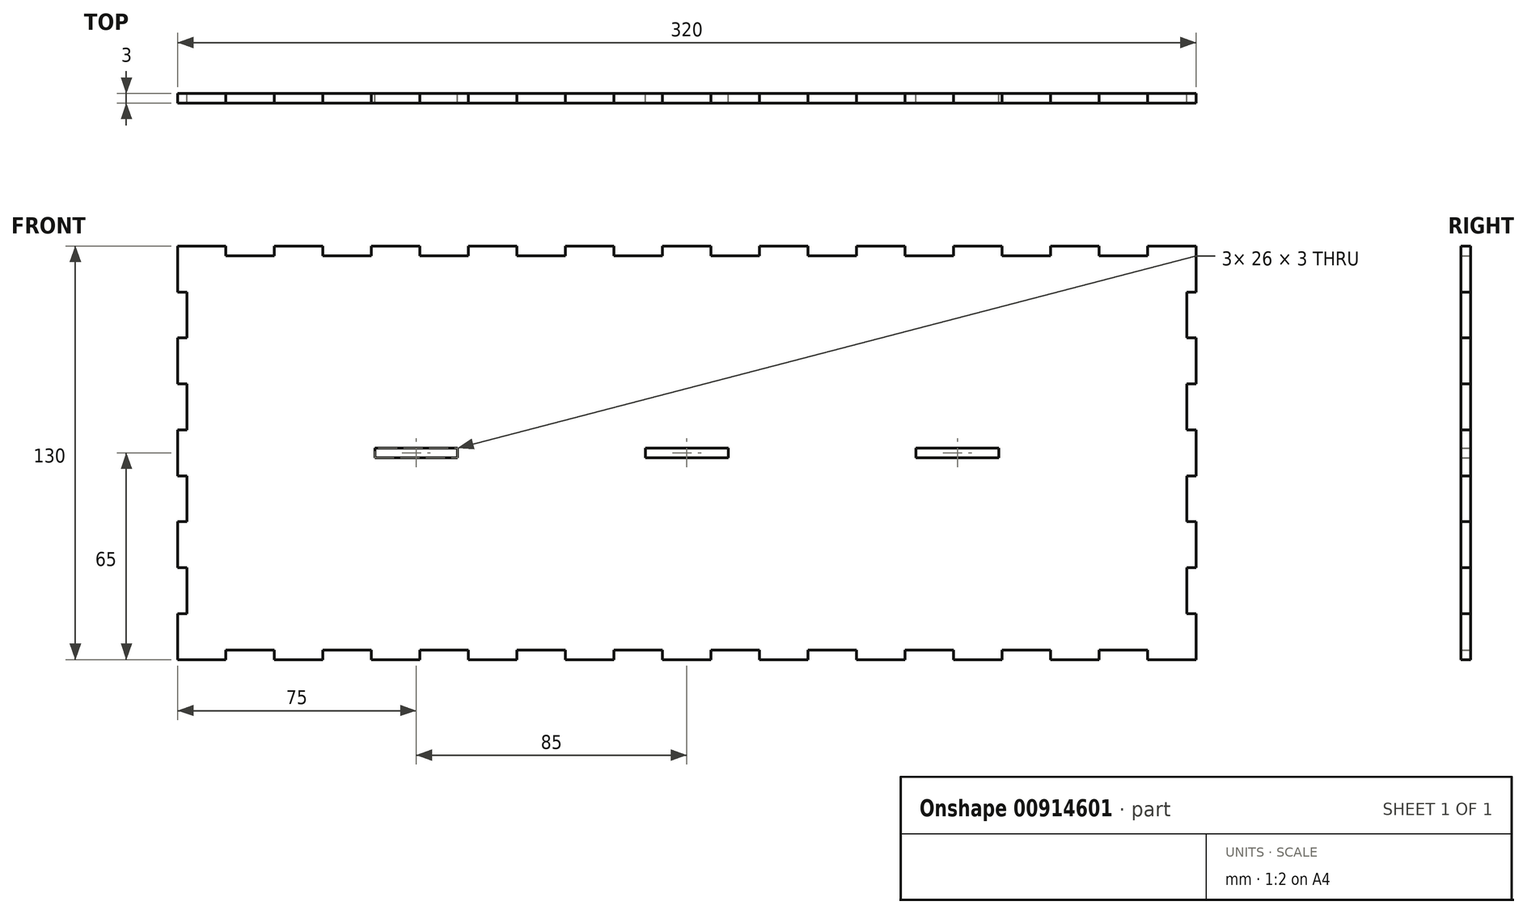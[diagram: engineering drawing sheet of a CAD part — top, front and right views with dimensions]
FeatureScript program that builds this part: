
annotation { "Feature Type Name" : "Feature", "Feature Type Description" : "" }
export const myFeature = defineFeature(function(context is Context, id is Id, definition is map)
    precondition{}
    {
        {
            var Q0;
            Q0=qCreatedBy(makeId("Front.planeOp"),FACE);
            var sketch = newSketch(context, id + "F0", { "sketchPlane" : qUnion([Q0])});
            skLineSegment(sketch, "E0.top", {"start": v(160, 65) * mm, "end": v(144.76, 65) * mm});
            skLineSegment(sketch, "E0.left", {"start": v(160, -65) * mm, "end": v(160, -62) * mm});
            skLineSegment(sketch, "E0.right", {"start": v(-160, -65) * mm, "end": v(-160, -50.56) * mm});
            skPoint(sketch, "E0.middle", {"position": v(0, 0) * mm});
            skLineSegment(sketch, "E1", {"start": v(-144.76, 62) * mm, "end": v(-129.52, 62) * mm});
            skLineSegment(sketch, "E2", {"start": v(-144.76, 65) * mm, "end": v(-144.76, 62) * mm});
            skLineSegment(sketch, "E3", {"start": v(-129.52, 65) * mm, "end": v(-129.52, 62) * mm});
            skLineSegment(sketch, "E4", {"start": v(-99.05, 65) * mm, "end": v(-99.05, 62) * mm});
            skLineSegment(sketch, "E5", {"start": v(-114.29, 65) * mm, "end": v(-114.29, 62) * mm});
            skLineSegment(sketch, "E6", {"start": v(-83.8, 65) * mm, "end": v(-83.8, 62) * mm});
            skLineSegment(sketch, "E7", {"start": v(-68.57, 65) * mm, "end": v(-68.57, 62) * mm});
            skLineSegment(sketch, "E8", {"start": v(-53.33, 65) * mm, "end": v(-53.33, 62) * mm});
            skLineSegment(sketch, "E9", {"start": v(-38.1, 65) * mm, "end": v(-38.1, 62) * mm});
            skLineSegment(sketch, "E10", {"start": v(-22.86, 65) * mm, "end": v(-22.86, 62) * mm});
            skLineSegment(sketch, "E11", {"start": v(22.86, 65) * mm, "end": v(22.86, 62) * mm});
            skLineSegment(sketch, "E12", {"start": v(-7.62, 65) * mm, "end": v(-7.62, 62) * mm});
            skLineSegment(sketch, "E13", {"start": v(7.62, 65) * mm, "end": v(7.62, 62) * mm});
            skLineSegment(sketch, "E14", {"start": v(38.1, 65) * mm, "end": v(38.1, 62) * mm});
            skLineSegment(sketch, "E15", {"start": v(53.33, 65) * mm, "end": v(53.33, 62) * mm});
            skLineSegment(sketch, "E16", {"start": v(68.57, 65) * mm, "end": v(68.57, 62) * mm});
            skLineSegment(sketch, "E17", {"start": v(83.8, 65) * mm, "end": v(83.8, 62) * mm});
            skLineSegment(sketch, "E18", {"start": v(99.05, 65) * mm, "end": v(99.05, 62) * mm});
            skLineSegment(sketch, "E19", {"start": v(114.29, 65) * mm, "end": v(114.29, 62) * mm});
            skLineSegment(sketch, "E20", {"start": v(129.52, 65) * mm, "end": v(129.52, 62) * mm});
            skLineSegment(sketch, "E21", {"start": v(144.76, 65) * mm, "end": v(144.76, 62) * mm});
            skLineSegment(sketch, "E22.trimOffspring", {"start": v(-144.76, 65) * mm, "end": v(-160, 65) * mm});
            skLineSegment(sketch, "E23.trimOffspring", {"start": v(-114.29, 62) * mm, "end": v(-99.05, 62) * mm});
            skLineSegment(sketch, "E24.trimOffspring", {"start": v(-114.29, 65) * mm, "end": v(-129.52, 65) * mm});
            skLineSegment(sketch, "E25.trimOffspring", {"start": v(-83.8, 62) * mm, "end": v(-68.57, 62) * mm});
            skLineSegment(sketch, "E26.trimOffspring", {"start": v(-83.8, 65) * mm, "end": v(-99.05, 65) * mm});
            skLineSegment(sketch, "E27.trimOffspring", {"start": v(-53.33, 62) * mm, "end": v(-38.1, 62) * mm});
            skLineSegment(sketch, "E28.trimOffspring", {"start": v(-53.33, 65) * mm, "end": v(-68.57, 65) * mm});
            skLineSegment(sketch, "E29.trimOffspring", {"start": v(-22.86, 62) * mm, "end": v(-7.62, 62) * mm});
            skLineSegment(sketch, "E30.trimOffspring", {"start": v(-22.86, 65) * mm, "end": v(-38.1, 65) * mm});
            skLineSegment(sketch, "E31.trimOffspring", {"start": v(7.62, 62) * mm, "end": v(22.86, 62) * mm});
            skLineSegment(sketch, "E32.trimOffspring", {"start": v(7.62, 65) * mm, "end": v(-7.62, 65) * mm});
            skLineSegment(sketch, "E33.trimOffspring", {"start": v(38.1, 62) * mm, "end": v(53.33, 62) * mm});
            skLineSegment(sketch, "E34.trimOffspring", {"start": v(38.1, 65) * mm, "end": v(22.86, 65) * mm});
            skLineSegment(sketch, "E35.trimOffspring", {"start": v(68.57, 62) * mm, "end": v(83.8, 62) * mm});
            skLineSegment(sketch, "E36.trimOffspring", {"start": v(68.57, 65) * mm, "end": v(53.33, 65) * mm});
            skLineSegment(sketch, "E37.trimOffspring", {"start": v(99.05, 62) * mm, "end": v(114.29, 62) * mm});
            skLineSegment(sketch, "E38.trimOffspring", {"start": v(99.05, 65) * mm, "end": v(83.8, 65) * mm});
            skLineSegment(sketch, "E39.trimOffspring", {"start": v(129.52, 62) * mm, "end": v(144.76, 62) * mm});
            skLineSegment(sketch, "E40.trimOffspring", {"start": v(129.52, 65) * mm, "end": v(114.29, 65) * mm});
            skLineSegment(sketch, "E41.MirrorCS", {"start": v(-38.1, -65) * mm, "end": v(-38.1, -62) * mm});
            skLineSegment(sketch, "E42.MirrorCS", {"start": v(-7.62, -65) * mm, "end": v(-7.62, -62) * mm});
            skLineSegment(sketch, "E43.MirrorCS", {"start": v(-22.86, -65) * mm, "end": v(-22.86, -62) * mm});
            skLineSegment(sketch, "E44.MirrorCS", {"start": v(53.33, -65) * mm, "end": v(53.33, -62) * mm});
            skLineSegment(sketch, "E45.MirrorCS", {"start": v(99.05, -65) * mm, "end": v(99.05, -62) * mm});
            skLineSegment(sketch, "E46.MirrorCS", {"start": v(-114.29, -65) * mm, "end": v(-114.29, -62) * mm});
            skLineSegment(sketch, "E47.MirrorCS", {"start": v(38.1, -65) * mm, "end": v(38.1, -62) * mm});
            skLineSegment(sketch, "E48.MirrorCS", {"start": v(-99.05, -65) * mm, "end": v(-99.05, -62) * mm});
            skLineSegment(sketch, "E49.MirrorCS", {"start": v(-68.57, -65) * mm, "end": v(-68.57, -62) * mm});
            skLineSegment(sketch, "E50.MirrorCS", {"start": v(-129.52, -65) * mm, "end": v(-129.52, -62) * mm});
            skLineSegment(sketch, "E51.MirrorCS", {"start": v(114.29, -65) * mm, "end": v(114.29, -62) * mm});
            skLineSegment(sketch, "E52.MirrorCS", {"start": v(-144.76, -65) * mm, "end": v(-144.76, -62) * mm});
            skLineSegment(sketch, "E53.MirrorCS", {"start": v(83.8, -65) * mm, "end": v(83.8, -62) * mm});
            skLineSegment(sketch, "E54.MirrorCS", {"start": v(129.52, -65) * mm, "end": v(129.52, -62) * mm});
            skLineSegment(sketch, "E55.MirrorCS", {"start": v(7.62, -65) * mm, "end": v(7.62, -62) * mm});
            skLineSegment(sketch, "E56.MirrorCS", {"start": v(144.76, -65) * mm, "end": v(144.76, -62) * mm});
            skLineSegment(sketch, "E57.MirrorCS", {"start": v(68.57, -65) * mm, "end": v(68.57, -62) * mm});
            skLineSegment(sketch, "E58.MirrorCS", {"start": v(22.86, -65) * mm, "end": v(22.86, -62) * mm});
            skLineSegment(sketch, "E59.MirrorCS", {"start": v(-83.8, -65) * mm, "end": v(-83.8, -62) * mm});
            skLineSegment(sketch, "E60.MirrorCS", {"start": v(-53.33, -65) * mm, "end": v(-53.33, -62) * mm});
            skLineSegment(sketch, "E61.MirrorCS", {"start": v(-22.86, -62) * mm, "end": v(-7.62, -62) * mm});
            skLineSegment(sketch, "E62.MirrorCS", {"start": v(-144.76, -65) * mm, "end": v(-160, -65) * mm});
            skLineSegment(sketch, "E63.MirrorCS", {"start": v(-22.86, -65) * mm, "end": v(-38.1, -65) * mm});
            skLineSegment(sketch, "E64.MirrorCS", {"start": v(-53.33, -62) * mm, "end": v(-38.1, -62) * mm});
            skLineSegment(sketch, "E65.MirrorCS", {"start": v(-144.76, -62) * mm, "end": v(-129.52, -62) * mm});
            skLineSegment(sketch, "E66.MirrorCS", {"start": v(129.52, -62) * mm, "end": v(144.76, -62) * mm});
            skLineSegment(sketch, "E67.MirrorCS", {"start": v(-114.29, -62) * mm, "end": v(-99.05, -62) * mm});
            skLineSegment(sketch, "E68.MirrorCS", {"start": v(7.62, -65) * mm, "end": v(-7.62, -65) * mm});
            skLineSegment(sketch, "E69.MirrorCS", {"start": v(38.1, -62) * mm, "end": v(53.33, -62) * mm});
            skLineSegment(sketch, "E70.MirrorCS", {"start": v(68.57, -62) * mm, "end": v(83.8, -62) * mm});
            skLineSegment(sketch, "E71.MirrorCS", {"start": v(99.05, -62) * mm, "end": v(114.29, -62) * mm});
            skLineSegment(sketch, "E72.MirrorCS", {"start": v(68.57, -65) * mm, "end": v(53.33, -65) * mm});
            skLineSegment(sketch, "E73.MirrorCS", {"start": v(-114.29, -65) * mm, "end": v(-129.52, -65) * mm});
            skLineSegment(sketch, "E74.MirrorCS", {"start": v(99.05, -65) * mm, "end": v(83.8, -65) * mm});
            skLineSegment(sketch, "E75.MirrorCS", {"start": v(129.52, -65) * mm, "end": v(114.29, -65) * mm});
            skLineSegment(sketch, "E76.MirrorCS", {"start": v(-53.33, -65) * mm, "end": v(-68.57, -65) * mm});
            skLineSegment(sketch, "E77.MirrorCS", {"start": v(-83.8, -62) * mm, "end": v(-68.57, -62) * mm});
            skLineSegment(sketch, "E78.MirrorCS", {"start": v(38.1, -65) * mm, "end": v(22.86, -65) * mm});
            skLineSegment(sketch, "E79.MirrorCS", {"start": v(-83.8, -65) * mm, "end": v(-99.05, -65) * mm});
            skLineSegment(sketch, "E80.MirrorCS", {"start": v(7.62, -62) * mm, "end": v(22.86, -62) * mm});
            skLineSegment(sketch, "E81.MirrorCS", {"start": v(160, -65) * mm, "end": v(144.76, -65) * mm});
            skLineSegment(sketch, "E82", {"start": v(-157, 50.56) * mm, "end": v(-157, 36.11) * mm});
            skLineSegment(sketch, "E83", {"start": v(-160, 50.56) * mm, "end": v(-157, 50.56) * mm});
            skLineSegment(sketch, "E84", {"start": v(-160, 36.11) * mm, "end": v(-157, 36.11) * mm});
            skLineSegment(sketch, "E85", {"start": v(-160, 21.67) * mm, "end": v(-157, 21.67) * mm});
            skLineSegment(sketch, "E86", {"start": v(-160, 7.22) * mm, "end": v(-157, 7.22) * mm});
            skLineSegment(sketch, "E87", {"start": v(-160, -7.22) * mm, "end": v(-157, -7.22) * mm});
            skLineSegment(sketch, "E88", {"start": v(-160, -21.67) * mm, "end": v(-157, -21.67) * mm});
            skLineSegment(sketch, "E89", {"start": v(-160, -36.11) * mm, "end": v(-157, -36.11) * mm});
            skLineSegment(sketch, "E90", {"start": v(-160, -50.56) * mm, "end": v(-157, -50.56) * mm});
            skLineSegment(sketch, "E91.trimOffspring", {"start": v(-160, 50.56) * mm, "end": v(-160, 65) * mm});
            skLineSegment(sketch, "E92.trimOffspring", {"start": v(-157, 21.67) * mm, "end": v(-157, 7.22) * mm});
            skLineSegment(sketch, "E93.trimOffspring", {"start": v(-160, 21.67) * mm, "end": v(-160, 36.11) * mm});
            skLineSegment(sketch, "E94.trimOffspring", {"start": v(-157, -7.22) * mm, "end": v(-157, -21.67) * mm});
            skLineSegment(sketch, "E95.trimOffspring", {"start": v(-160, -7.22) * mm, "end": v(-160, 7.22) * mm});
            skLineSegment(sketch, "E96.trimOffspring", {"start": v(-157, -36.11) * mm, "end": v(-157, -50.56) * mm});
            skLineSegment(sketch, "E97.trimOffspring", {"start": v(-160, -36.11) * mm, "end": v(-160, -21.67) * mm});
            skLineSegment(sketch, "E98.trimOffspring", {"start": v(160, 62) * mm, "end": v(160, 65) * mm});
            skLineSegment(sketch, "E99.MirrorCS", {"start": v(160, -36.11) * mm, "end": v(157, -36.11) * mm});
            skLineSegment(sketch, "E100.MirrorCS", {"start": v(160, 50.56) * mm, "end": v(157, 50.56) * mm});
            skLineSegment(sketch, "E101.MirrorCS", {"start": v(160, -21.67) * mm, "end": v(157, -21.67) * mm});
            skLineSegment(sketch, "E102.MirrorCS", {"start": v(160, -7.22) * mm, "end": v(157, -7.22) * mm});
            skLineSegment(sketch, "E103.MirrorCS", {"start": v(160, -50.56) * mm, "end": v(157, -50.56) * mm});
            skLineSegment(sketch, "E104.MirrorCS", {"start": v(160, 21.67) * mm, "end": v(157, 21.67) * mm});
            skLineSegment(sketch, "E105.MirrorCS", {"start": v(160, 36.11) * mm, "end": v(157, 36.11) * mm});
            skLineSegment(sketch, "E106.MirrorCS", {"start": v(160, 7.22) * mm, "end": v(157, 7.22) * mm});
            skLineSegment(sketch, "E107.MirrorCS", {"start": v(160, 21.67) * mm, "end": v(160, 36.11) * mm});
            skLineSegment(sketch, "E108.MirrorCS", {"start": v(160, -36.11) * mm, "end": v(160, -21.67) * mm});
            skLineSegment(sketch, "E109.MirrorCS", {"start": v(160, -7.22) * mm, "end": v(160, 7.22) * mm});
            skLineSegment(sketch, "E110.MirrorCS", {"start": v(157, 21.67) * mm, "end": v(157, 7.22) * mm});
            skLineSegment(sketch, "E111.MirrorCS", {"start": v(157, -7.22) * mm, "end": v(157, -21.67) * mm});
            skLineSegment(sketch, "E112.MirrorCS", {"start": v(160, 50.56) * mm, "end": v(160, 65) * mm});
            skLineSegment(sketch, "E113.MirrorCS", {"start": v(157, 50.56) * mm, "end": v(157, 36.11) * mm});
            skLineSegment(sketch, "E114.MirrorCS", {"start": v(160, -65) * mm, "end": v(160, -50.56) * mm});
            skLineSegment(sketch, "E115.MirrorCS", {"start": v(157, -36.11) * mm, "end": v(157, -50.56) * mm});
            skLineSegment(sketch, "E116.bottom", {"start": v(98, -1.5) * mm, "end": v(72, -1.5) * mm});
            skLineSegment(sketch, "E116.top", {"start": v(98, 1.5) * mm, "end": v(72, 1.5) * mm});
            skLineSegment(sketch, "E116.left", {"start": v(160, -1.5) * mm, "end": v(160, 1.5) * mm});
            skLineSegment(sketch, "E116.right", {"start": v(-160, -1.5) * mm, "end": v(-160, 1.5) * mm});
            skLineSegment(sketch, "E117", {"start": v(-13, 1.5) * mm, "end": v(-13, -1.5) * mm});
            skLineSegment(sketch, "E118", {"start": v(13, 1.5) * mm, "end": v(13, -1.5) * mm});
            skLineSegment(sketch, "E119", {"start": v(-98, 1.5) * mm, "end": v(-98, -1.5) * mm});
            skLineSegment(sketch, "E120", {"start": v(-72, 1.5) * mm, "end": v(-72, -1.5) * mm});
            skLineSegment(sketch, "E121.MirrorCS", {"start": v(72, 1.5) * mm, "end": v(72, -1.5) * mm});
            skLineSegment(sketch, "E122.MirrorCS", {"start": v(98, 1.5) * mm, "end": v(98, -1.5) * mm});
            skLineSegment(sketch, "E123.trimOffspring", {"start": v(-72, 1.5) * mm, "end": v(-98, 1.5) * mm});
            skLineSegment(sketch, "E124.trimOffspring", {"start": v(-72, -1.5) * mm, "end": v(-98, -1.5) * mm});
            skLineSegment(sketch, "E125.trimOffspring", {"start": v(13, -1.5) * mm, "end": v(-13, -1.5) * mm});
            skLineSegment(sketch, "E126.trimOffspring", {"start": v(13, 1.5) * mm, "end": v(-13, 1.5) * mm});
            skSolve(sketch);
        }
        {
            var Q0;
            {var subQ3=sQuery(id+"F0.wireOp",EDGE,"E0.top");Q0=makeQuery(id+"F0.imprint","IMPRINT",FACE,{"disambiguationData":[TD([[makeQuery(id+"F0.imprint","IMPRINT",EDGE,{"derivedFrom":subQ3}),1.0]])]});}
            extrude(context, id + "F1", {"entities" : qUnion([Q0]), "depth" : 3 * mm, "offsetDistance" : 25 * mm});
        }
    });
